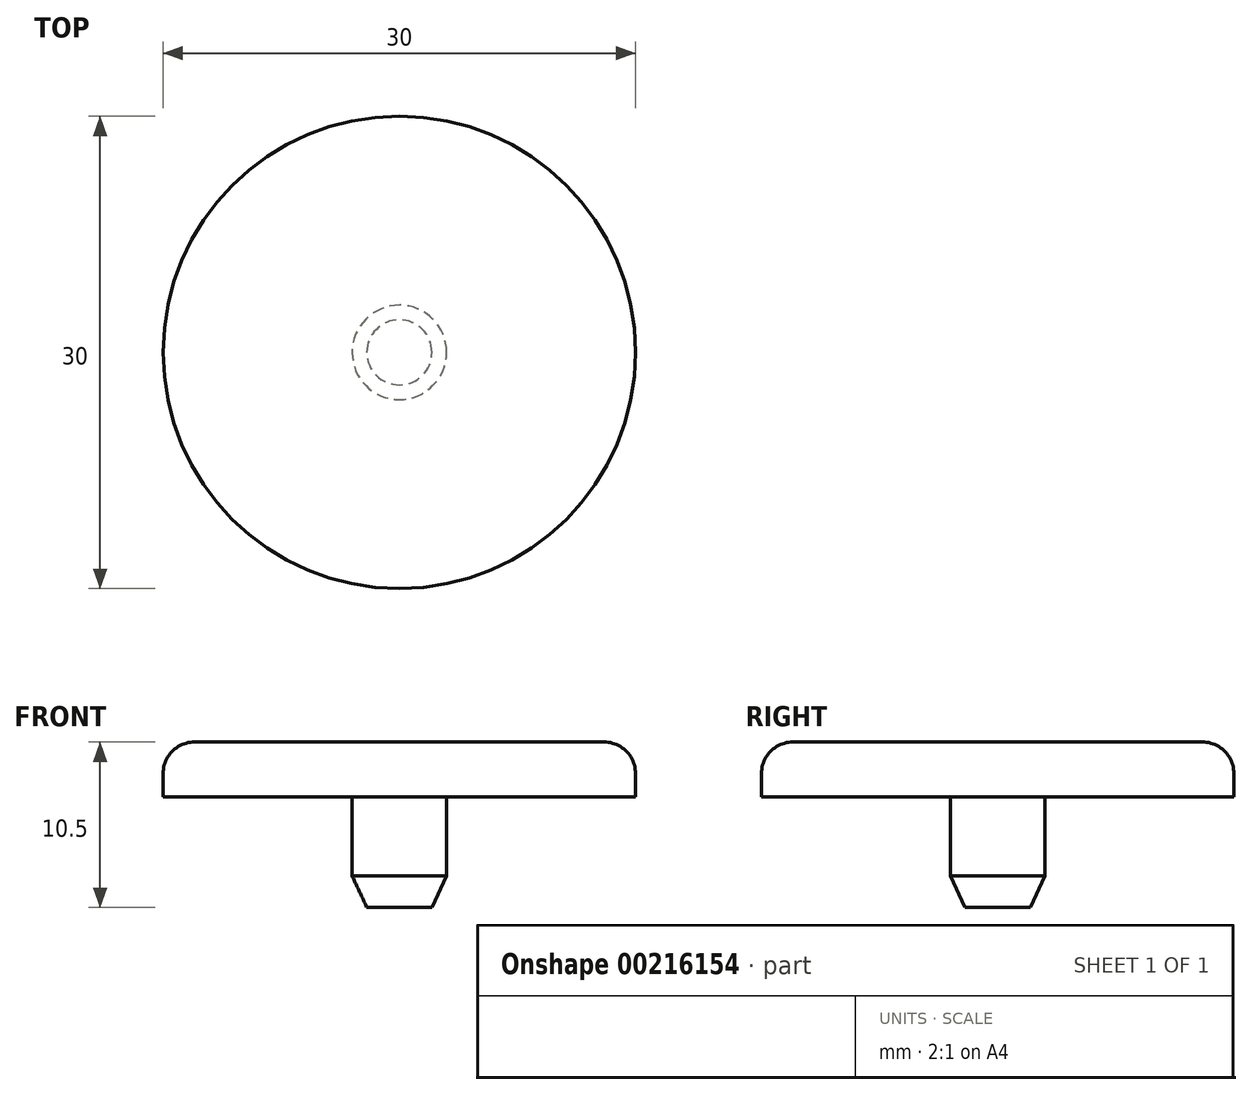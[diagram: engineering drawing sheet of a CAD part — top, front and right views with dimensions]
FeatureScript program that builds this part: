
annotation { "Feature Type Name" : "Feature", "Feature Type Description" : "" }
export const myFeature = defineFeature(function(context is Context, id is Id, definition is map)
    precondition{}
    {
        {
            var Q0;
            Q0=qCreatedBy(makeId("Front.planeOp"),FACE);
            var sketch = newSketch(context, id + "F0", { "sketchPlane" : qUnion([Q0])});
            skLineSegment(sketch, "E0", {"start": v(0, 0) * mm, "end": v(0, 9.1) * mm, "construction": true});
            skLineSegment(sketch, "E1.bottom", {"start": v(-3, 0) * mm, "end": v(-15, 0) * mm});
            skLineSegment(sketch, "E1.top", {"start": v(-3, 3.5) * mm, "end": v(-13, 3.5) * mm});
            skLineSegment(sketch, "E1.right", {"start": v(-15, 0) * mm, "end": v(-15, 1.5) * mm});
            skPoint(sketch, "E2.visualSharp", {"position": v(-15, 3.5) * mm});
            skArc(sketch, "E2.filletArc", {"start": v(-13, 3.5) * mm, "mid": v(-14.41, 2.91) * mm, "end": v(-15, 1.5) * mm});
            skLineSegment(sketch, "E3", {"start": v(-3, 0) * mm, "end": v(-3, -5) * mm});
            skLineSegment(sketch, "E4", {"start": v(-3, -5) * mm, "end": v(-2.07, -7) * mm});
            skLineSegment(sketch, "E5", {"start": v(-2.07, -7) * mm, "end": v(0, -7) * mm});
            skLineSegment(sketch, "E6", {"start": v(0, -7) * mm, "end": v(0, 3.5) * mm});
            skLineSegment(sketch, "E7", {"start": v(0, 3.5) * mm, "end": v(-3, 3.5) * mm});
            skSolve(sketch);
        }
        {
            var Q0;
            Q0=makeQuery(id+"F0.imprint","IMPRINT",FACE,{"disambiguationData":[TD([[makeQuery(id+"F0.imprint","IMPRINT",EDGE,{"derivedFrom":sQuery(id+"F0.wireOp",EDGE,"E1.bottom")}),-1.0]])]});
            var Q1;
            Q1=sQuery(id+"F0.wireOp",EDGE,"E0");
            revolve(context, id + "F1", {"entities" : qUnion([Q0]), "axis" : qUnion([Q1]), "revolveType" : RevolveType.FULL});
        }
    });
